# Revit family: RS292
name_source: partatom
category: Sanitärinstallationen
units: mm (PartAtom-declared; Revit-internal decimal feet)

## family parameters
Arbeitsebenenbasiert = Nein
Beim Laden mit Abzugskörper schneiden = Nein
Bemaßung runder Anschluss = Durchmesser verwenden
Gemeinsam genutzt = Nein
Immer vertikal = Ja
Raumberechnungspunkt = Nein
Teiletyp = Normal

## types (4) — shared parameters
Baugruppenkennzeichen = D2030300
Hersteller = Resitec
RS_AVol-Absch = 200 mm  [stored 0.656168 ft]
RS_AVol-H = 2 mm  [stored 0.00656168 ft]
RS_AVol-KB = 400 mm  [stored 1.31234 ft]
RS_Manufacture = Resitec
RS_URL = https://resitec.ch
RS_VOLin001 = 125 mm  [stored 0.410105 ft]
RS_dia001 = 129 mm  [stored 0.423228 ft]
RS_dia002 = 130 mm  [stored 0.426509 ft]
RS_dim001 = 170 mm  [stored 0.557743 ft]
RS_dim002 = 150 mm
RS_dim003 = 25 mm  [stored 0.082021 ft]
RS_s = 1 mm  [stored 0.00328084 ft]
RS_s001 = 2 mm  [stored 0.00656168 ft]
URL = https://www.resitec.ch
zero-valued in all types: Anschlusswert DU L/s, RS_DN2, Vorgabe-Ansicht

## per-type parameters (varying)
| type | RS_DN1 | RS_DN1d |
| DN40 | 40 mm  [stored 0.131234 ft] | 42 mm  [stored 0.137795 ft] |
| DN50 | 50 mm  [stored 0.164042 ft] | 54 mm  [stored 0.177165 ft] |
| DN70 | 70 mm  [stored 0.229659 ft] | 76 mm  [stored 0.249344 ft] |
| DN80 | 90 mm  [stored 0.295276 ft] | 89 mm |

note: [stored X ft] marks values corroborated as IEEE doubles in the binary element streams (Revit-internal decimal feet)

## geometry (parser evidence)
native form markers: Blend x12
no freeform markers — native parametric forms only
